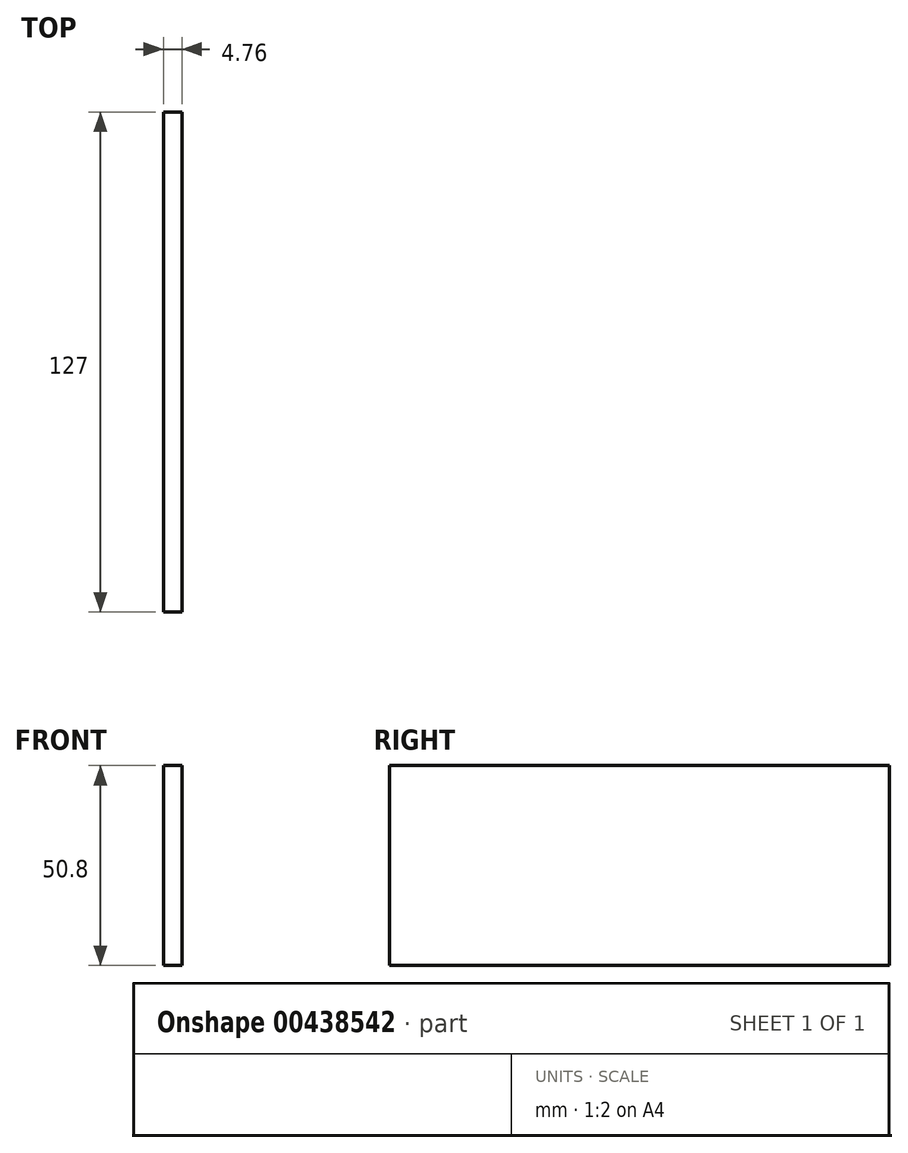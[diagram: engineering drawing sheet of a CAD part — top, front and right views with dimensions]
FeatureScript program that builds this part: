
annotation { "Feature Type Name" : "Feature", "Feature Type Description" : "" }
export const myFeature = defineFeature(function(context is Context, id is Id, definition is map)
    precondition{}
    {
        {
            var Q0;
            Q0=qCreatedBy(makeId("Right.planeOp"),FACE);
            var sketch = newSketch(context, id + "F0", { "sketchPlane" : qUnion([Q0])});
            skLineSegment(sketch, "E0.bottom", {"start": v(-24.08, 3.77) * mm, "end": v(102.92, 3.77) * mm});
            skLineSegment(sketch, "E0.top", {"start": v(-24.08, -47.03) * mm, "end": v(102.92, -47.03) * mm});
            skLineSegment(sketch, "E0.left", {"start": v(-24.08, 3.77) * mm, "end": v(-24.08, -47.03) * mm});
            skLineSegment(sketch, "E0.right", {"start": v(102.92, 3.77) * mm, "end": v(102.92, -47.03) * mm});
            skSolve(sketch);
        }
        {
            var Q0;
            Q0=makeQuery(id+"F0.imprint","IMPRINT",FACE,{"disambiguationData":[TD([[makeQuery(id+"F0.imprint","IMPRINT",EDGE,{"derivedFrom":sQuery(id+"F0.wireOp",EDGE,"E0.bottom")}),-1.0]])]});
            extrude(context, id + "F1", {"entities" : qUnion([Q0]), "depth" : 4.76 * mm});
        }
    });
